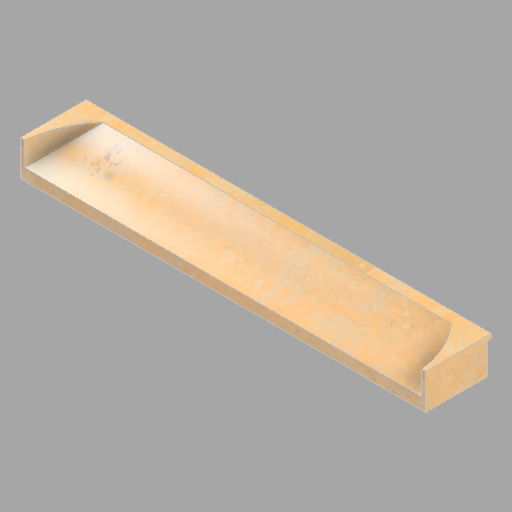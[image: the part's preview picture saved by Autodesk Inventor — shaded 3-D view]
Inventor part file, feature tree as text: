
AUTODESK INVENTOR PART (.ipt)
format: ipt  version: 2022.2 (Build 262287010, 287A)  size: 229,888 bytes
history: native  units: in
note: dims shown in document units (in); Inventor stores cm internally (conversion verified against a paired STEP export)
features: other x1, direct_edit x1, revolve x1
ambient origin geometry x8: Origin, YZ Plane, XZ Plane, XY Plane, X Axis, Y Axis, Z Axis, Center Point
bodies: Solid1 (feature_tree)
feature tree (3):
  other  "North (4) (3)"
  direct_edit  "Direct Edit1"
  revolve  "Rotate1"  Angle=90.0deg
